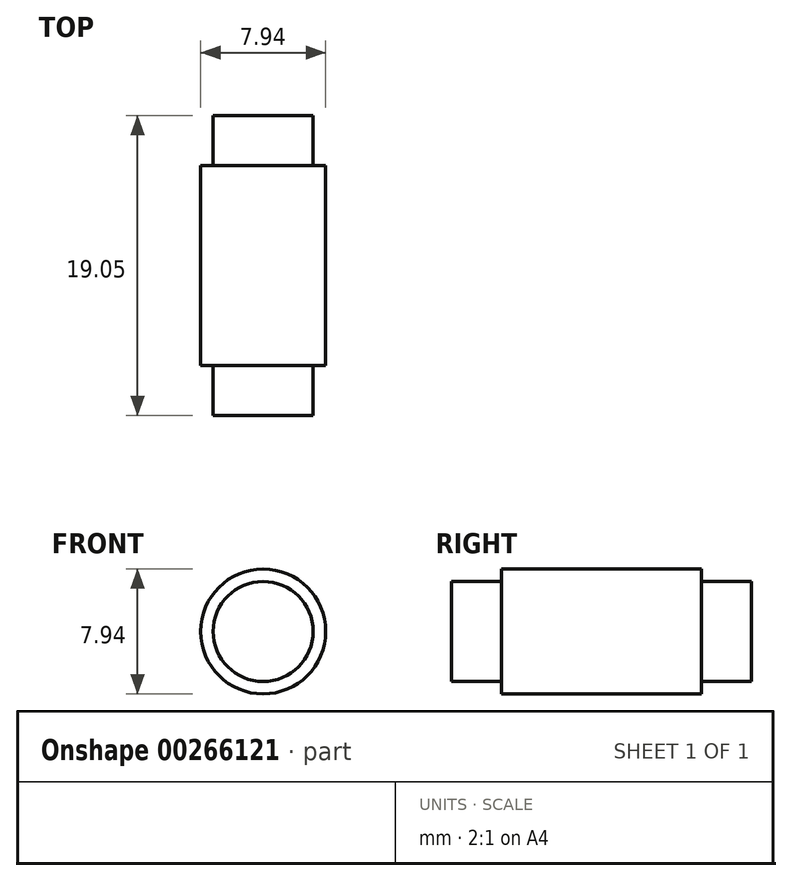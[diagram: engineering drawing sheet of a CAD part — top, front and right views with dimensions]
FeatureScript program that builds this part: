
annotation { "Feature Type Name" : "Feature", "Feature Type Description" : "" }
export const myFeature = defineFeature(function(context is Context, id is Id, definition is map)
    precondition{}
    {
        {
            var Q0;
            Q0=qCreatedBy(makeId("Front.planeOp"),FACE);
            var sketch = newSketch(context, id + "F0", { "sketchPlane" : qUnion([Q0])});
            skCircle(sketch, "E0", {"center": v(0, 0) * mm, "radius": 3.17 * mm});
            skSolve(sketch);
        }
        {
            var Q0;
            Q0=makeQuery(id+"F0.imprint","IMPRINT",FACE,{"disambiguationData":[TD([[makeQuery(id+"F0.imprint","IMPRINT",EDGE,{"derivedFrom":sQuery(id+"F0.wireOp",EDGE,"E0")}),1.0]])]});
            extrude(context, id + "F1", {"entities" : qUnion([Q0]), "depth" : 3.17 * mm});
        }
        {
            var Q0;
            Q0=makeQuery(id+"F1.opExtrude","CAP_FACE",FACE,{"disambiguationData":[OSD([sQuery(id+"F0.wireOp",EDGE,"E0")])],"isStart":false});
            var sketch = newSketch(context, id + "F2", { "sketchPlane" : qUnion([Q0])});
            skCircle(sketch, "E1", {"center": v(0, 0) * mm, "radius": 3.97 * mm});
            skSolve(sketch);
        }
        {
            var Q0;
            Q0 = qSketchRegion(id + "F2", true);
            extrude(context, id + "F3", {"entities" : qUnion([Q0]), "operationType" : NewBodyOperationType.ADD, "depth" : 12.7 * mm});
        }
        {
            var Q0;
            Q0=makeQuery(id+"F3.opExtrude","CAP_FACE",FACE,{"disambiguationData":[OSD([sQuery(id+"F2.wireOp",EDGE,"E1")])],"isStart":false});
            var sketch = newSketch(context, id + "F4", { "sketchPlane" : qUnion([Q0])});
            skCircle(sketch, "E2.0.0", {"center": v(0, 0) * mm, "radius": 3.17 * mm});
            skSolve(sketch);
        }
        {
            var Q0;
            Q0 = qSketchRegion(id + "F4", true);
            extrude(context, id + "F5", {"entities" : qUnion([Q0]), "operationType" : NewBodyOperationType.ADD, "depth" : 3.17 * mm});
        }
    });
